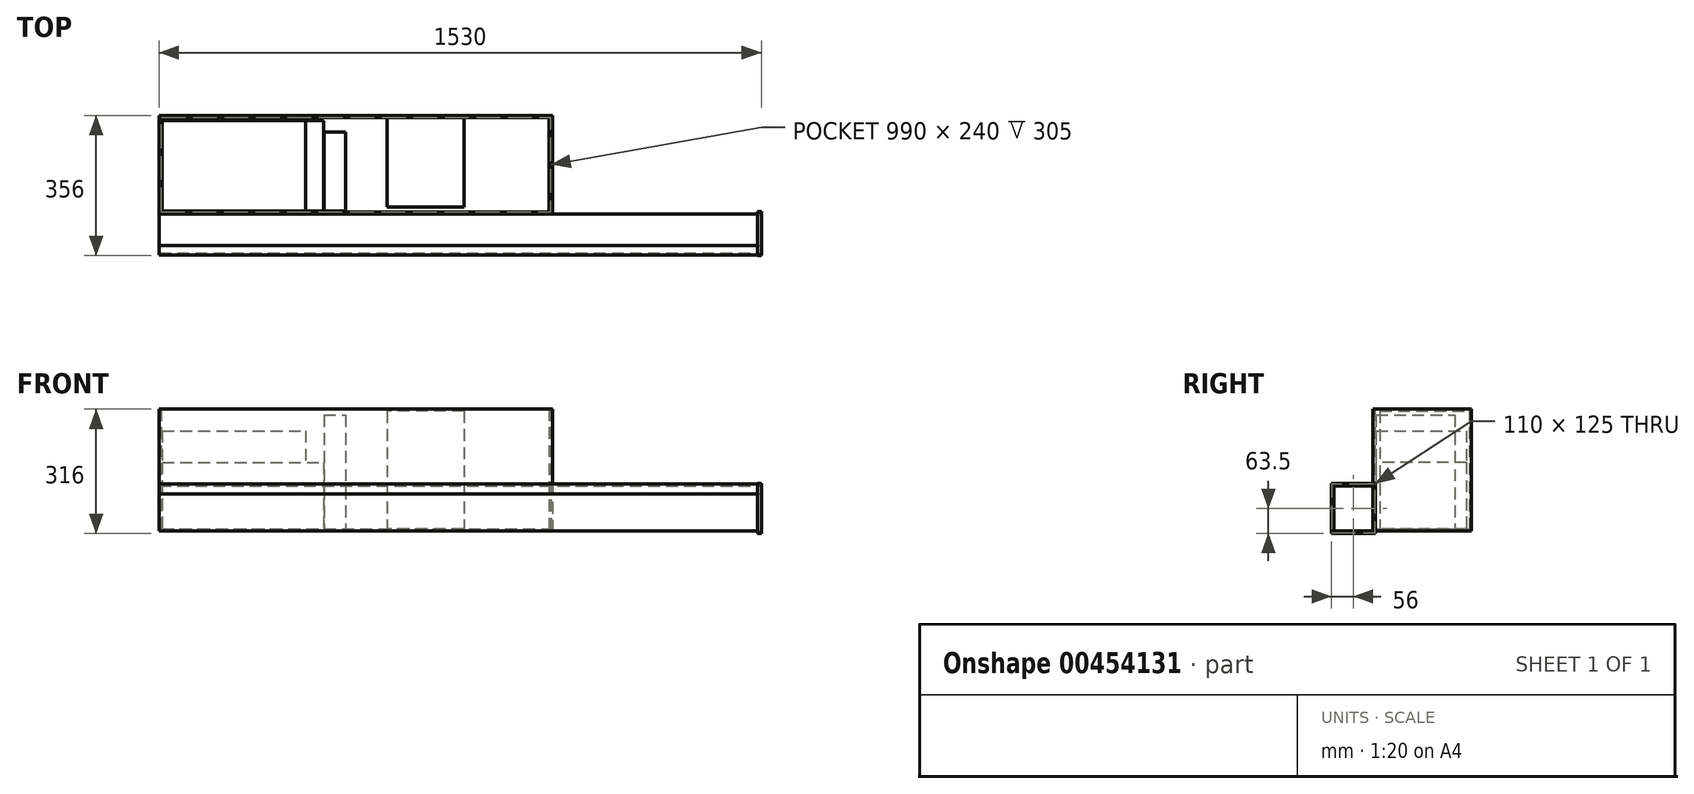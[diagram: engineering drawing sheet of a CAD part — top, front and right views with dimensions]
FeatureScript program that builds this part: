
annotation { "Feature Type Name" : "Feature", "Feature Type Description" : "" }
export const myFeature = defineFeature(function(context is Context, id is Id, definition is map)
    precondition{}
    {
        {
            var Q0;
            Q0=qCreatedBy(makeId("Top.planeOp"),FACE);
            var sketch = newSketch(context, id + "F0", { "sketchPlane" : qUnion([Q0])});
            skLineSegment(sketch, "E0.bottom", {"start": v(0, 0) * mm, "end": v(1000, 0) * mm});
            skLineSegment(sketch, "E0.top", {"start": v(0, 250) * mm, "end": v(1000, 250) * mm});
            skLineSegment(sketch, "E0.left", {"start": v(0, 0) * mm, "end": v(0, 250) * mm});
            skLineSegment(sketch, "E0.right", {"start": v(1000, 0) * mm, "end": v(1000, 250) * mm});
            skSolve(sketch);
        }
        {
            var Q0;
            Q0=qSketchRegion(id+"F0",true);
            extrude(context, id + "F1", {"entities" : qUnion([Q0]), "depth" : 310 * mm});
        }
        {
            var Q0;
            Q0=makeQuery(id+"F1.opExtrude","CAP_FACE",FACE,{"disambiguationData":[OSD([sQuery(id+"F0.wireOp",EDGE,"E0.bottom"),sQuery(id+"F0.wireOp",EDGE,"E0.top"),sQuery(id+"F0.wireOp",EDGE,"E0.left"),sQuery(id+"F0.wireOp",EDGE,"E0.right")])],"isStart":false});
            shell(context, id + "F2", {"entities" : qUnion([Q0]), "thickness" : 5 * mm});
        }
        {
            var Q0;
            Q0=makeQuery(id+"F2.opShell","OFFSET_FACE",FACE,{"disambiguationData":[OSD([sQuery(id+"F0.wireOp",EDGE,"E0.bottom"),sQuery(id+"F0.wireOp",EDGE,"E0.top"),sQuery(id+"F0.wireOp",EDGE,"E0.left"),sQuery(id+"F0.wireOp",EDGE,"E0.right")])]});
            var sketch = newSketch(context, id + "F3", { "sketchPlane" : qUnion([Q0])});
            skLineSegment(sketch, "E1.bottom", {"start": v(7.5, 237.5) * mm, "end": v(417.5, 237.5) * mm});
            skLineSegment(sketch, "E1.top", {"start": v(7.5, 7.5) * mm, "end": v(417.5, 7.5) * mm});
            skLineSegment(sketch, "E1.left", {"start": v(7.5, 237.5) * mm, "end": v(7.5, 7.5) * mm});
            skLineSegment(sketch, "E1.right", {"start": v(417.5, 237.5) * mm, "end": v(417.5, 7.5) * mm});
            skSolve(sketch);
        }
        {
            var Q0;
            Q0=qSketchRegion(id+"F3",true);
            extrude(context, id + "F4", {"entities" : qUnion([Q0]), "depth" : 170 * mm});
        }
        {
            var Q0;
            Q0=makeQuery(id+"F4.opExtrude","CAP_FACE",FACE,{"disambiguationData":[OSD([sQuery(id+"F3.wireOp",EDGE,"E1.bottom"),sQuery(id+"F3.wireOp",EDGE,"E1.top"),sQuery(id+"F3.wireOp",EDGE,"E1.left"),sQuery(id+"F3.wireOp",EDGE,"E1.right")])],"isStart":false});
            var sketch = newSketch(context, id + "F5", { "sketchPlane" : qUnion([Q0])});
            skLineSegment(sketch, "E2.bottom", {"start": v(7.5, 7.5) * mm, "end": v(372.5, 7.5) * mm});
            skLineSegment(sketch, "E2.top", {"start": v(7.5, 237.5) * mm, "end": v(372.5, 237.5) * mm});
            skLineSegment(sketch, "E2.left", {"start": v(7.5, 7.5) * mm, "end": v(7.5, 237.5) * mm});
            skLineSegment(sketch, "E2.right", {"start": v(372.5, 7.5) * mm, "end": v(372.5, 237.5) * mm});
            skSolve(sketch);
        }
        {
            var Q0;
            Q0=qSketchRegion(id+"F5",true);
            extrude(context, id + "F6", {"entities" : qUnion([Q0]), "depth" : 80 * mm});
        }
        {
            var Q0;
            Q0=makeQuery(id+"F2.opShell","OFFSET_FACE",FACE,{"disambiguationData":[OSD([sQuery(id+"F0.wireOp",EDGE,"E0.bottom"),sQuery(id+"F0.wireOp",EDGE,"E0.top"),sQuery(id+"F0.wireOp",EDGE,"E0.left"),sQuery(id+"F0.wireOp",EDGE,"E0.right")])]});
            var sketch = newSketch(context, id + "F7", { "sketchPlane" : qUnion([Q0])});
            skLineSegment(sketch, "E3.bottom", {"start": v(418.5, 7.5) * mm, "end": v(473.5, 7.5) * mm});
            skLineSegment(sketch, "E3.top", {"start": v(418.5, 207.5) * mm, "end": v(473.5, 207.5) * mm});
            skLineSegment(sketch, "E3.left", {"start": v(418.5, 7.5) * mm, "end": v(418.5, 207.5) * mm});
            skLineSegment(sketch, "E3.right", {"start": v(473.5, 7.5) * mm, "end": v(473.5, 207.5) * mm});
            skSolve(sketch);
        }
        {
            var Q0;
            Q0=qSketchRegion(id+"F7",true);
            extrude(context, id + "F8", {"entities" : qUnion([Q0]), "depth" : 290 * mm});
        }
        {
            var Q0;
            Q0=makeQuery(id+"F2.opShell","OFFSET_FACE",FACE,{"disambiguationData":[OSD([sQuery(id+"F0.wireOp",EDGE,"E0.bottom"),sQuery(id+"F0.wireOp",EDGE,"E0.top"),sQuery(id+"F0.wireOp",EDGE,"E0.left"),sQuery(id+"F0.wireOp",EDGE,"E0.right")])]});
            var sketch = newSketch(context, id + "F9", { "sketchPlane" : qUnion([Q0])});
            skLineSegment(sketch, "E4.bottom", {"start": v(774.11, 17.7) * mm, "end": v(579.11, 17.7) * mm});
            skLineSegment(sketch, "E4.top", {"start": v(774.11, 247.7) * mm, "end": v(579.11, 247.7) * mm});
            skLineSegment(sketch, "E4.left", {"start": v(774.11, 17.7) * mm, "end": v(774.11, 247.7) * mm});
            skLineSegment(sketch, "E4.right", {"start": v(579.11, 17.7) * mm, "end": v(579.11, 247.7) * mm});
            skSolve(sketch);
        }
        {
            var Q0;
            Q0=qSketchRegion(id+"F9",true);
            extrude(context, id + "F10", {"entities" : qUnion([Q0]), "depth" : 300 * mm});
        }
        {
            var Q0;
            Q0=qCreatedBy(makeId("Top.planeOp"),FACE);
            var sketch = newSketch(context, id + "F11", { "sketchPlane" : qUnion([Q0])});
            skLineSegment(sketch, "E5.bottom", {"start": v(0, 0) * mm, "end": v(1530, 0) * mm});
            skLineSegment(sketch, "E5.top", {"start": v(0, -100) * mm, "end": v(1530, -100) * mm});
            skLineSegment(sketch, "E5.left", {"start": v(0, 0) * mm, "end": v(0, -100) * mm});
            skLineSegment(sketch, "E5.right", {"start": v(1530, 0) * mm, "end": v(1530, -100) * mm});
            skSolve(sketch);
        }
        {
            var Q0;
            Q0=makeQuery(id+"F11.imprint","IMPRINT",FACE,{"disambiguationData":[TD([[makeQuery(id+"F11.imprint","IMPRINT",EDGE,{"derivedFrom":sQuery(id+"F11.wireOp",EDGE,"E5.bottom")}),-1.0]])]});
            extrude(context, id + "F12", {"entities" : qUnion([Q0]), "depth" : 115 * mm});
        }
        {
            var Q0;
            Q0=makeQuery(id+"F2.opShell","OFFSET_FACE",FACE,{"disambiguationData":[OSD([sQuery(id+"F0.wireOp",EDGE,"E0.right")])]});
            var sketch = newSketch(context, id + "F13", { "sketchPlane" : qUnion([Q0])});
            skLineSegment(sketch, "E6.bottom", {"start": v(-245, 310) * mm, "end": v(-5, 310) * mm});
            skLineSegment(sketch, "E6.top", {"start": v(-245, 5) * mm, "end": v(-5, 5) * mm});
            skLineSegment(sketch, "E6.left", {"start": v(-245, 310) * mm, "end": v(-245, 5) * mm});
            skLineSegment(sketch, "E6.right", {"start": v(-5, 310) * mm, "end": v(-5, 5) * mm});
            skSolve(sketch);
        }
        {
            var Q0;
            Q0=qSketchRegion(id+"F13",true);
            extrude(context, id + "F14", {"entities" : qUnion([Q0]), "depth" : 5 * mm});
        }
        {
            var Q0;
            Q0=makeQuery(id+"F12.opExtrude","SWEPT_FACE",FACE,{"disambiguationData":[OSD([sQuery(id+"F11.wireOp",EDGE,"E5.right")])]});
            var sketch = newSketch(context, id + "F15", { "sketchPlane" : qUnion([Q0])});
            skLineSegment(sketch, "E7.bottom", {"start": v(-100, 115) * mm, "end": v(-80, 115) * mm});
            skLineSegment(sketch, "E7.left", {"start": v(-100, 115) * mm, "end": v(-100, 95) * mm});
            skLineSegment(sketch, "E8.bottom", {"start": v(-105, 120) * mm, "end": v(-80, 120) * mm});
            skLineSegment(sketch, "E8.top", {"start": v(-105, 95) * mm, "end": v(-100, 95) * mm});
            skLineSegment(sketch, "E8.left", {"start": v(-105, 120) * mm, "end": v(-105, 95) * mm});
            skLineSegment(sketch, "E8.right", {"start": v(-80, 120) * mm, "end": v(-80, 115) * mm});
            skSolve(sketch);
        }
        {
            var Q0;
            Q0=qSketchRegion(id+"F15",true);
            var Q1;
            Q1=makeQuery(id+"F12.opExtrude","SWEPT_FACE",FACE,{"disambiguationData":[OSD([sQuery(id+"F11.wireOp",EDGE,"E5.left")])]});
            extrude(context, id + "F16", {"entities" : qUnion([Q0]), "endBound" : BoundingType.UP_TO_SURFACE, "oppositeDirection" : true, "endBoundEntityFace" : qUnion([Q1]), "depth" : 25 * mm});
        }
        {
            var Q0;
            Q0=makeQuery(id+"F16.opExtrude","CAP_FACE",FACE,{"disambiguationData":[OSD([sQuery(id+"F15.wireOp",EDGE,"E7.bottom"),sQuery(id+"F15.wireOp",EDGE,"E7.left"),sQuery(id+"F15.wireOp",EDGE,"E8.bottom"),sQuery(id+"F15.wireOp",EDGE,"E8.top"),sQuery(id+"F15.wireOp",EDGE,"E8.left"),sQuery(id+"F15.wireOp",EDGE,"E8.right")])],"isStart":true});
            var sketch = newSketch(context, id + "F17", { "sketchPlane" : qUnion([Q0])});
            skLineSegment(sketch, "E9.bottom", {"start": v(-105, 120) * mm, "end": v(5, 120) * mm});
            skLineSegment(sketch, "E9.top", {"start": v(-105, -5) * mm, "end": v(5, -5) * mm});
            skLineSegment(sketch, "E9.left", {"start": v(-105, 120) * mm, "end": v(-105, -5) * mm});
            skLineSegment(sketch, "E9.right", {"start": v(5, 120) * mm, "end": v(5, -5) * mm});
            skPoint(sketch, "E9.middle", {"position": v(-50, 57.5) * mm});
            skLineSegment(sketch, "E10.0", {"start": v(6, 121) * mm, "end": v(6, -6) * mm});
            skLineSegment(sketch, "E10.1", {"start": v(-106, 121) * mm, "end": v(6, 121) * mm});
            skLineSegment(sketch, "E10.2", {"start": v(-106, 121) * mm, "end": v(-106, -6) * mm});
            skLineSegment(sketch, "E10.3", {"start": v(-106, -6) * mm, "end": v(6, -6) * mm});
            skSolve(sketch);
        }
        {
            var Q0;
            Q0=qSketchRegion(id+"F17",true);
            extrude(context, id + "F18", {"entities" : qUnion([Q0]), "oppositeDirection" : true, "depth" : 10 * mm});
        }
    });
